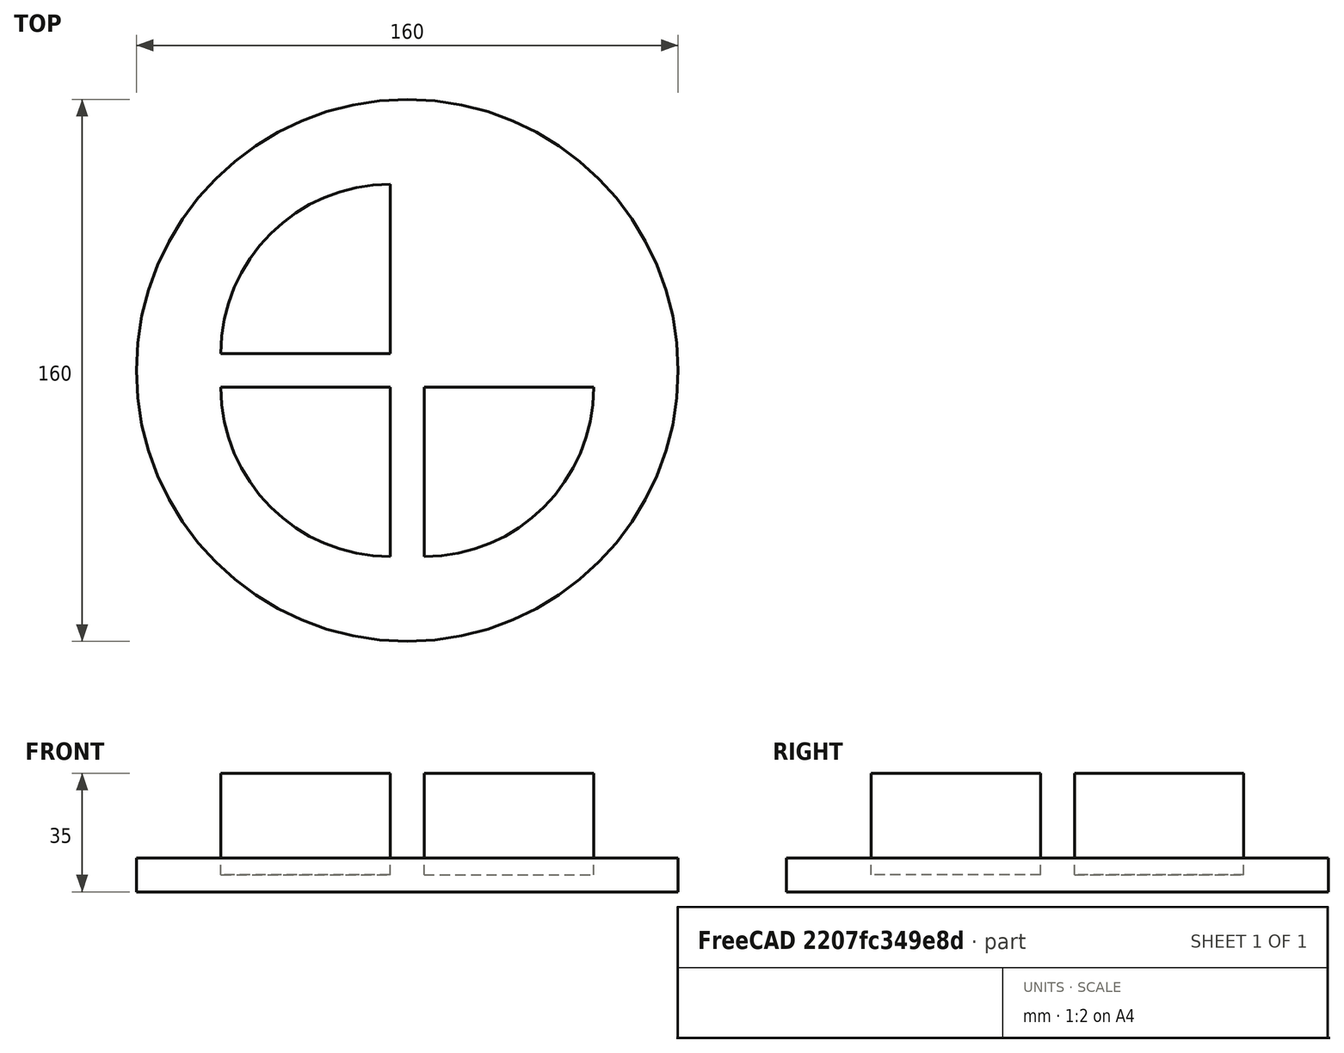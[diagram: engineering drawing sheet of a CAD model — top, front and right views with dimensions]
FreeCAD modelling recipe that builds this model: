
FCSTD DOCUMENT  (FreeCAD 1.0R38806 (Git))
Label: Ej tipo tarta
License: All rights reserved
LicenseURL: http://en.wikipedia.org/wiki/All_rights_reserved
objects: Part::Cylinder×4
note: 4 computed .brp shape members not serialized (recipe doc carries the construction recipe); baked Part::Feature solids carry a one-line shape summary decoded from their .brp

FEATURE [Part::Cylinder] Cylinder  label="Plato"
  Angle = 360
  AttacherType = Attacher::AttachEngine3D
  FirstAngle = 0
  Height = 10
  Placement = pos=(0,0,-5) rot=(0,0,1;0rad)
  Radius = 80
  SecondAngle = 0
FEATURE [Part::Cylinder] Cylinder001  label="Trozo1"
  Angle = 90
  AttacherType = Attacher::AttachEngine3D
  FirstAngle = 0
  Height = 30
  Placement = pos=(-5,5,0) rot=(0,0,1;1.5708rad)
  Radius = 50
  SecondAngle = 0
FEATURE [Part::Cylinder] Cylinder002  label="Trozo2"
  Angle = 90
  AttacherType = Attacher::AttachEngine3D
  FirstAngle = 0
  Height = 30
  Placement = pos=(-5,-5,0) rot=(0,0,1;3.14159rad)
  Radius = 50
  SecondAngle = 0
FEATURE [Part::Cylinder] Cylinder003  label="Trozo3"
  Angle = 90
  AttacherType = Attacher::AttachEngine3D
  FirstAngle = 0
  Height = 30
  Placement = pos=(5,-5,0) rot=(0,0,1;4.71239rad)
  Radius = 50
  SecondAngle = 0
